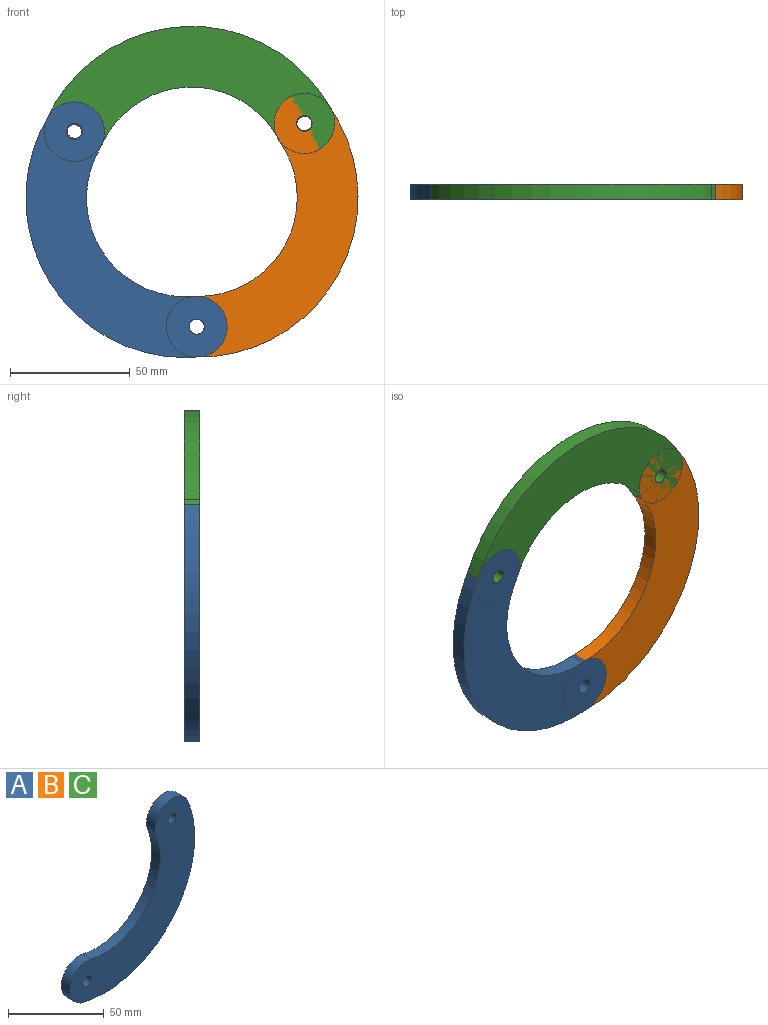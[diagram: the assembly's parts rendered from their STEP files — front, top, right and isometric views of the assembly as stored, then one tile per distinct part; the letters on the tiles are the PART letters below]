
ASSEMBLY  parts=3 mates=3
PART A: 8 faces, bbox 92.2x6.4x99.6 mm
  f0: cylinder r=12.72mm len=24.06mm, axis (0,1,0), area 246.7mm2, adj f1,f3,f4,f5
  f1: cylinder r=41.27mm len=56.72mm, axis (0,1,0), area 575.2mm2, adj f0,f2,f4,f5
  f2: cylinder r=12.71mm len=24.85mm, axis (0,1,0), area 248.6mm2, adj f1,f3,f4,f5
  f3: cylinder r=66.67mm len=92.65mm, axis (0,1,0), area 941.1mm2, adj f0,f2,f4,f5
  f4: plane 99.6x92.23mm, normal (0,-1,0), area 3453.1mm2, adj f0,f1,f2,f3,f6,f7
  f5: plane 99.6x92.23mm, normal (0,1,0), area 3453.1mm2, adj f0,f1,f2,f3,f6,f7
  f6: cylinder r=3.17mm len=6.35mm, axis (0,1,0), area 126.7mm2, adj f4,f5
  f7: cylinder r=3.17mm len=6.35mm, axis (0,1,0), area 126.7mm2, adj f4,f5
PART B: same geometry as A
PART C: same geometry as A
PLACE A rot(axis=(0,1,0),106.9deg) t=(-269.21,13.86,-8.32)mm
PLACE B rot(axis=(0,-1,0),12.9deg) t=(-182.85,13.86,-8.94)mm
PLACE C rot(axis=(0,-1,0),132.8deg) t=(-225.36,13.86,66.51)mm
MATE pin_slot C.f0 <-> A.f2  axis (0,-1,0) through (-274.84,7.51,42.82)mm
MATE pin_slot A.f0 <-> B.f2  axis (0,-1,0) through (-223.8,7.51,-39.1)mm
MATE pin_slot C.f2 <-> B.f0  axis (0,-1,0) through (-178.79,7.51,46.06)mm
